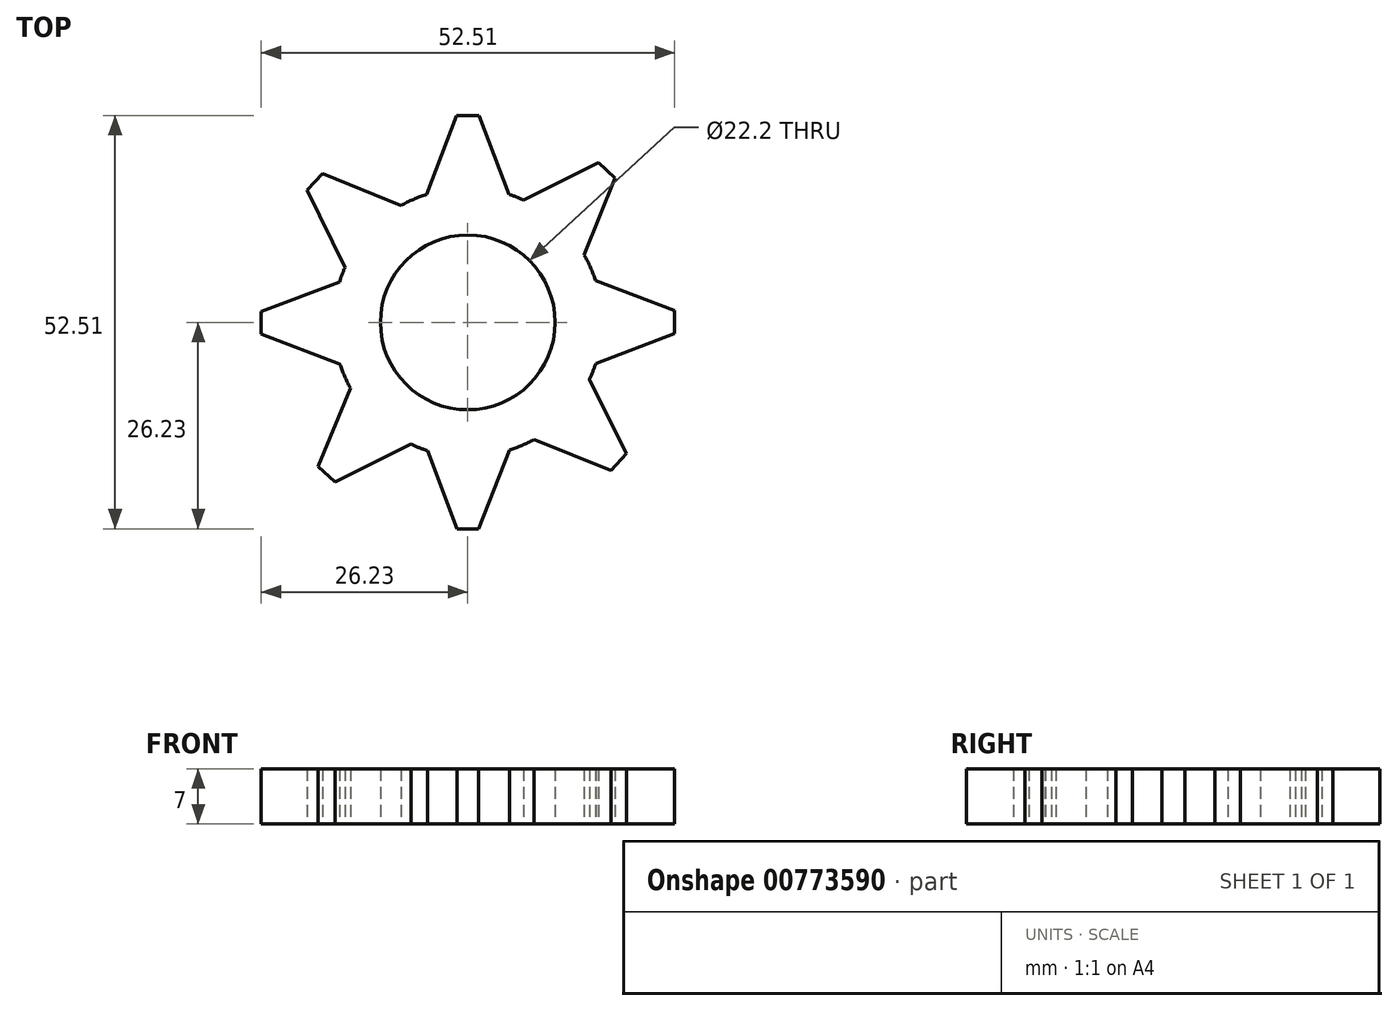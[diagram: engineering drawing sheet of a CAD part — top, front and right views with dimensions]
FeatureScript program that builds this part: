
annotation { "Feature Type Name" : "Feature", "Feature Type Description" : "" }
export const myFeature = defineFeature(function(context is Context, id is Id, definition is map)
    precondition{}
    {
        {
            var Q0;
            Q0=qCreatedBy(makeId("Top.planeOp"),FACE);
            var sketch = newSketch(context, id + "F0", { "sketchPlane" : qUnion([Q0])});
            skCircle(sketch, "E0", {"center": v(0, 0) * mm, "radius": 11.1 * mm});
            skCircle(sketch, "E1", {"center": v(0, 0) * mm, "radius": 17.08 * mm});
            skLineSegment(sketch, "E2", {"start": v(-1.45, 26.28) * mm, "end": v(1.45, 26.28) * mm});
            skLineSegment(sketch, "E3", {"start": v(1.45, 26.28) * mm, "end": v(5.23, 16.26) * mm});
            skLineSegment(sketch, "E4", {"start": v(-1.45, 26.28) * mm, "end": v(-5.23, 16.26) * mm});
            skLineSegment(sketch, "E5", {"start": v(1.37, -26.23) * mm, "end": v(-1.37, -26.23) * mm});
            skLineSegment(sketch, "E6", {"start": v(-1.37, -26.23) * mm, "end": v(-5.15, -16.21) * mm});
            skLineSegment(sketch, "E7", {"start": v(1.37, -26.23) * mm, "end": v(5.3, -16.21) * mm});
            skLineSegment(sketch, "E8", {"start": v(0, 26.28) * mm, "end": v(0, 17.08) * mm});
            skLineSegment(sketch, "E9", {"start": v(0, -26.23) * mm, "end": v(0, -17.08) * mm});
            skLineSegment(sketch, "E10", {"start": v(-26.23, -1.5) * mm, "end": v(-26.23, 1.4) * mm});
            skLineSegment(sketch, "E11", {"start": v(-26.23, 1.4) * mm, "end": v(-16.21, 5.18) * mm});
            skLineSegment(sketch, "E12", {"start": v(-26.23, -1.5) * mm, "end": v(-16.2, -5.28) * mm});
            skLineSegment(sketch, "E13", {"start": v(26.28, 1.48) * mm, "end": v(26.28, -1.42) * mm});
            skLineSegment(sketch, "E14", {"start": v(26.28, -1.42) * mm, "end": v(16.26, -5.2) * mm});
            skLineSegment(sketch, "E15", {"start": v(26.28, 1.48) * mm, "end": v(16.24, 5.29) * mm});
            skLineSegment(sketch, "E16", {"start": v(-26.23, -0.05) * mm, "end": v(-17.03, -0.05) * mm});
            skLineSegment(sketch, "E17", {"start": v(26.28, 0.03) * mm, "end": v(17.13, 0.03) * mm});
            skLineSegment(sketch, "E18", {"start": v(-20.39, 16.8) * mm, "end": v(-18.47, 18.88) * mm});
            skLineSegment(sketch, "E19", {"start": v(-18.47, 18.88) * mm, "end": v(-8.48, 14.83) * mm});
            skLineSegment(sketch, "E20", {"start": v(-20.39, 16.8) * mm, "end": v(-15.6, 6.97) * mm});
            skLineSegment(sketch, "E21", {"start": v(20.17, -16.69) * mm, "end": v(18.18, -18.85) * mm});
            skLineSegment(sketch, "E22", {"start": v(18.18, -18.85) * mm, "end": v(8.25, -14.82) * mm});
            skLineSegment(sketch, "E23", {"start": v(20.17, -16.69) * mm, "end": v(15.36, -7.14) * mm});
            skLineSegment(sketch, "E24", {"start": v(-19.43, 17.84) * mm, "end": v(-12.6, 11.53) * mm});
            skLineSegment(sketch, "E25", {"start": v(19.18, -17.77) * mm, "end": v(12.52, -11.62) * mm});
            skLineSegment(sketch, "E26", {"start": v(-16.86, -20.3) * mm, "end": v(-18.99, -18.34) * mm});
            skLineSegment(sketch, "E27", {"start": v(-18.99, -18.34) * mm, "end": v(-14.91, -8.33) * mm});
            skLineSegment(sketch, "E28", {"start": v(-16.86, -20.3) * mm, "end": v(-7.22, -15.48) * mm});
            skLineSegment(sketch, "E29", {"start": v(16.6, 20.27) * mm, "end": v(18.74, 18.3) * mm});
            skLineSegment(sketch, "E30", {"start": v(18.74, 18.3) * mm, "end": v(14.7, 8.38) * mm});
            skLineSegment(sketch, "E31", {"start": v(16.6, 20.27) * mm, "end": v(7, 15.49) * mm});
            skLineSegment(sketch, "E32", {"start": v(-17.92, -19.32) * mm, "end": v(-11.68, -12.57) * mm});
            skLineSegment(sketch, "E33", {"start": v(17.67, 19.29) * mm, "end": v(11.46, 12.57) * mm});
            skSolve(sketch);
        }
        {
            var Q0;
            Q0 = qSketchRegion(id + "F0", true);
            extrude(context, id + "F1", {"entities" : qUnion([Q0]), "endBound" : BoundingType.SYMMETRIC, "depth" : 7 * mm, "offsetDistance" : 25.4 * mm});
        }
    });
